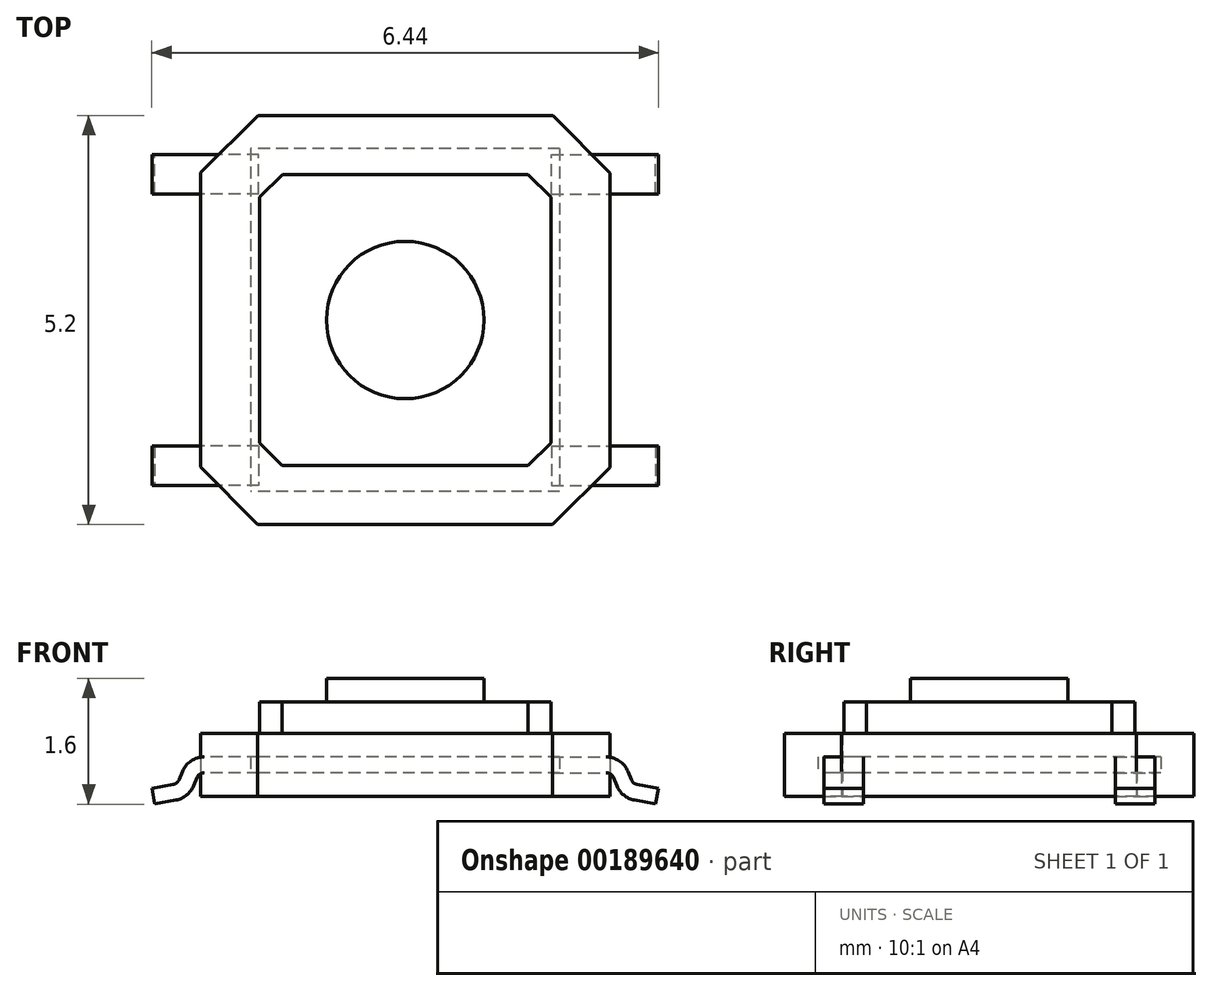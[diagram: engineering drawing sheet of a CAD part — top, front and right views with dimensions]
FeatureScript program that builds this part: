
annotation { "Feature Type Name" : "Feature", "Feature Type Description" : "" }
export const myFeature = defineFeature(function(context is Context, id is Id, definition is map)
    precondition{}
    {
        {
            var Q0;
            Q0=qCreatedBy(makeId("Top.planeOp"),FACE);
            var sketch = newSketch(context, id + "F0", { "sketchPlane" : qUnion([Q0])});
            skLineSegment(sketch, "E0", {"start": v(0, 2.6) * mm, "end": v(0, 0) * mm});
            skLineSegment(sketch, "E1", {"start": v(0, 2.6) * mm, "end": v(-1.87, 2.6) * mm});
            skLineSegment(sketch, "E2", {"start": v(-1.87, 2.6) * mm, "end": v(-2.6, 1.88) * mm});
            skLineSegment(sketch, "E3", {"start": v(-2.6, 1.88) * mm, "end": v(-2.6, 0) * mm});
            skLineSegment(sketch, "E4", {"start": v(-2.6, 0) * mm, "end": v(0, 0) * mm});
            skLineSegment(sketch, "E5.1.0", {"start": v(-1.88, -2.6) * mm, "end": v(0, -2.6) * mm});
            skLineSegment(sketch, "E5.1.1", {"start": v(-2.6, -1.87) * mm, "end": v(-1.88, -2.6) * mm});
            skLineSegment(sketch, "E5.1.3", {"start": v(0, -2.6) * mm, "end": v(0, 0) * mm});
            skLineSegment(sketch, "E5.1.4", {"start": v(-2.6, 0) * mm, "end": v(-2.6, -1.87) * mm});
            skLineSegment(sketch, "E5.2.0", {"start": v(2.6, -1.88) * mm, "end": v(2.6, 0) * mm});
            skLineSegment(sketch, "E5.2.1", {"start": v(1.87, -2.6) * mm, "end": v(2.6, -1.88) * mm});
            skLineSegment(sketch, "E5.2.2", {"start": v(0, -2.6) * mm, "end": v(0, 0) * mm});
            skLineSegment(sketch, "E5.2.3", {"start": v(2.6, 0) * mm, "end": v(0, 0) * mm});
            skLineSegment(sketch, "E5.2.4", {"start": v(0, -2.6) * mm, "end": v(1.87, -2.6) * mm});
            skLineSegment(sketch, "E5.3.0", {"start": v(1.88, 2.6) * mm, "end": v(0, 2.6) * mm});
            skLineSegment(sketch, "E5.3.1", {"start": v(2.6, 1.87) * mm, "end": v(1.88, 2.6) * mm});
            skLineSegment(sketch, "E5.3.2", {"start": v(2.6, 0) * mm, "end": v(0, 0) * mm});
            skLineSegment(sketch, "E5.3.4", {"start": v(2.6, 0) * mm, "end": v(2.6, 1.87) * mm});
            skPoint(sketch, "E5.center", {"position": v(0, 0) * mm});
            skSolve(sketch);
        }
        {
            var Q0;
            Q0=qSketchRegion(id+"F0",true);
            extrude(context, id + "F1", {"entities" : qUnion([Q0]), "depth" : 0.8 * mm});
        }
        {
            var Q0;
            Q0=makeQuery(id+"F1.opExtrude","CAP_FACE",FACE,{"disambiguationData":[OSD([sQuery(id+"F0.wireOp",EDGE,"E1"),sQuery(id+"F0.wireOp",EDGE,"E2"),sQuery(id+"F0.wireOp",EDGE,"E3"),sQuery(id+"F0.wireOp",EDGE,"E5.1.0"),sQuery(id+"F0.wireOp",EDGE,"E5.1.1"),sQuery(id+"F0.wireOp",EDGE,"E5.1.4"),sQuery(id+"F0.wireOp",EDGE,"E5.2.0"),sQuery(id+"F0.wireOp",EDGE,"E5.2.1"),sQuery(id+"F0.wireOp",EDGE,"E5.2.4"),sQuery(id+"F0.wireOp",EDGE,"E5.3.0"),sQuery(id+"F0.wireOp",EDGE,"E5.3.1"),sQuery(id+"F0.wireOp",EDGE,"E5.3.4")])],"isStart":false});
            var sketch = newSketch(context, id + "F2", { "sketchPlane" : qUnion([Q0])});
            skLineSegment(sketch, "E6.0", {"start": v(1.85, -1.56) * mm, "end": v(1.85, 1.56) * mm});
            skLineSegment(sketch, "E6.1", {"start": v(1.56, -1.85) * mm, "end": v(1.85, -1.56) * mm});
            skLineSegment(sketch, "E6.2", {"start": v(-1.56, -1.85) * mm, "end": v(1.56, -1.85) * mm});
            skLineSegment(sketch, "E6.3", {"start": v(-1.85, -1.56) * mm, "end": v(-1.56, -1.85) * mm});
            skLineSegment(sketch, "E6.4", {"start": v(-1.85, 1.56) * mm, "end": v(-1.85, -1.56) * mm});
            skLineSegment(sketch, "E6.5", {"start": v(1.85, 1.56) * mm, "end": v(1.56, 1.85) * mm});
            skLineSegment(sketch, "E6.6", {"start": v(-1.56, 1.85) * mm, "end": v(-1.85, 1.56) * mm});
            skLineSegment(sketch, "E6.7", {"start": v(1.56, 1.85) * mm, "end": v(-1.56, 1.85) * mm});
            skSolve(sketch);
        }
        {
            var Q0;
            Q0=qSketchRegion(id+"F2",true);
            extrude(context, id + "F3", {"entities" : qUnion([Q0]), "operationType" : NewBodyOperationType.ADD, "depth" : 0.4 * mm});
        }
        {
            var Q0;
            Q0=makeQuery(id+"F3.opExtrude","CAP_FACE",FACE,{"disambiguationData":[OSD([sQuery(id+"F2.wireOp",EDGE,"E6.0"),sQuery(id+"F2.wireOp",EDGE,"E6.1"),sQuery(id+"F2.wireOp",EDGE,"E6.2"),sQuery(id+"F2.wireOp",EDGE,"E6.3"),sQuery(id+"F2.wireOp",EDGE,"E6.4"),sQuery(id+"F2.wireOp",EDGE,"E6.5"),sQuery(id+"F2.wireOp",EDGE,"E6.6"),sQuery(id+"F2.wireOp",EDGE,"E6.7")])],"isStart":false});
            var sketch = newSketch(context, id + "F4", { "sketchPlane" : qUnion([Q0])});
            skCircle(sketch, "E7", {"center": v(0, 0) * mm, "radius": 1 * mm});
            skSolve(sketch);
        }
        {
            var Q0;
            Q0=qSketchRegion(id+"F4",true);
            extrude(context, id + "F5", {"entities" : qUnion([Q0]), "operationType" : NewBodyOperationType.ADD, "depth" : 0.3 * mm});
        }
        {
            var Q0;
            Q0=qCreatedBy(makeId("Top.planeOp"),FACE);
            cPlane(context, id + "F6", {"entities" : qUnion([Q0]), "cplaneType" : CPlaneType.OFFSET, "offset" : 0.3 * mm, "width" : 150 * mm, "height" : 150 * mm});
        }
        {
            var Q0;
            Q0=qCreatedBy(id+"F6.planeOp",FACE);
            var sketch = newSketch(context, id + "F7", { "sketchPlane" : qUnion([Q0])});
            skLineSegment(sketch, "E8.rect.bottom", {"start": v(1.96, 2.18) * mm, "end": v(-1.96, 2.18) * mm});
            skLineSegment(sketch, "E8.rect.top", {"start": v(1.96, -2.18) * mm, "end": v(-1.96, -2.18) * mm});
            skLineSegment(sketch, "E8.rect.left", {"start": v(1.96, 2.18) * mm, "end": v(1.96, -2.18) * mm});
            skLineSegment(sketch, "E8.rect.right", {"start": v(-1.96, 2.18) * mm, "end": v(-1.96, -2.18) * mm});
            skPoint(sketch, "E8.rect.middle", {"position": v(0, 0) * mm});
            skSolve(sketch);
        }
        {
            var Q0;
            Q0=qCreatedBy(makeId("Front.planeOp"),FACE);
            var sketch = newSketch(context, id + "F8", { "sketchPlane" : qUnion([Q0])});
            skLineSegment(sketch, "E9", {"start": v(1.86, 0.4) * mm, "end": v(2.55, 0.4) * mm});
            skLineSegment(sketch, "E10", {"start": v(2.74, 0.28) * mm, "end": v(2.78, 0.17) * mm});
            skLineSegment(sketch, "E11", {"start": v(2.93, 0.05) * mm, "end": v(3.2, 0) * mm});
            skPoint(sketch, "E12.visualSharp", {"position": v(2.68, 0.4) * mm});
            skArc(sketch, "E12.filletArc", {"start": v(2.74, 0.28) * mm, "mid": v(2.66, 0.37) * mm, "end": v(2.55, 0.4) * mm});
            skPoint(sketch, "E13.visualSharp", {"position": v(2.82, 0.07) * mm});
            skArc(sketch, "E13.filletArc", {"start": v(2.78, 0.17) * mm, "mid": v(2.84, 0.1) * mm, "end": v(2.93, 0.05) * mm});
            skSolve(sketch);
        }
        {
            var Q0;
            Q0=qSketchRegion(id+"F7",true);
            extrude(context, id + "F9", {"entities" : qUnion([Q0]), "depth" : 0.2 * mm});
        }
        {
            var Q0;
            Q0=sQuery(id+"F8.wireOp",EDGE,"E9");
            var Q1;
            Q1=sQuery(id+"F8.wireOp",VERTEX,"E9.start");
            cPlane(context, id + "F10", {"entities" : qUnion([Q0, Q1]), "cplaneType" : CPlaneType.LINE_POINT, "offset" : 150 * mm, "width" : 150 * mm, "height" : 150 * mm});
        }
        {
            var Q0;
            Q0=qCreatedBy(id+"F10.planeOp",FACE);
            var sketch = newSketch(context, id + "F11", { "sketchPlane" : qUnion([Q0])});
            skLineSegment(sketch, "E14.rect.bottom", {"start": v(-0.25, 0.3) * mm, "end": v(0.25, 0.3) * mm});
            skLineSegment(sketch, "E14.rect.top", {"start": v(-0.25, 0.5) * mm, "end": v(0.25, 0.5) * mm});
            skLineSegment(sketch, "E14.rect.left", {"start": v(-0.25, 0.3) * mm, "end": v(-0.25, 0.5) * mm});
            skLineSegment(sketch, "E14.rect.right", {"start": v(0.25, 0.3) * mm, "end": v(0.25, 0.5) * mm});
            skPoint(sketch, "E14.rect.middle", {"position": v(0, 0.4) * mm});
            skSolve(sketch);
        }
        {
            var Q0;
            Q0=qSketchRegion(id+"F11",true);
            var Q1;
            Q1=qConstructionFilter(qBodyType(qCreatedBy(id+"F8",EDGE),BodyType.WIRE),ConstructionObject.NO);
            sweep(context, id + "F12", {"profiles" : qUnion([Q0]), "path" : qUnion([Q1])});
        }
        {
            var Q0;
            Q0=makeQuery(id+"F12.opSweep","SWEPT_BODY",BODY,{"disambiguationData":[OSD([sQuery(id+"F8.wireOp",EDGE,"E9"),sQuery(id+"F11.wireOp",EDGE,"E14.rect.bottom"),sQuery(id+"F11.wireOp",EDGE,"E14.rect.top"),sQuery(id+"F11.wireOp",EDGE,"E14.rect.left"),sQuery(id+"F11.wireOp",EDGE,"E14.rect.right")])]});
            transform(context, id + "F13", {"entities" : qUnion([Q0]), "transformType" : TransformType.TRANSLATION_3D, "dx" : 0 * mm, "dy" : 1.85 * mm, "dz" : 0 * mm, "makeCopy" : false});
        }
        {
            var Q0;
            Q0=makeQuery(id+"F12.opSweep","SWEPT_BODY",BODY,{"disambiguationData":[OSD([sQuery(id+"F8.wireOp",EDGE,"E9"),sQuery(id+"F11.wireOp",EDGE,"E14.rect.bottom"),sQuery(id+"F11.wireOp",EDGE,"E14.rect.top"),sQuery(id+"F11.wireOp",EDGE,"E14.rect.left"),sQuery(id+"F11.wireOp",EDGE,"E14.rect.right")])]});
            var Q1;
            Q1=qCreatedBy(makeId("Right.planeOp"),FACE);
            mirror(context, id + "F14", {"entities" : qUnion([Q0]), "mirrorPlane" : qUnion([Q1])});
        }
        {
            var Q0;
            Q0=makeQuery(id+"F14.opPattern","COPY",BODY,{"derivedFrom":makeQuery(id+"F12.opSweep","SWEPT_BODY",BODY,{"disambiguationData":[OSD([sQuery(id+"F8.wireOp",EDGE,"E9"),sQuery(id+"F11.wireOp",EDGE,"E14.rect.bottom"),sQuery(id+"F11.wireOp",EDGE,"E14.rect.top"),sQuery(id+"F11.wireOp",EDGE,"E14.rect.left"),sQuery(id+"F11.wireOp",EDGE,"E14.rect.right")])]}),"instanceName":"1"});
            var Q1;
            Q1=makeQuery(id+"F12.opSweep","SWEPT_BODY",BODY,{"disambiguationData":[OSD([sQuery(id+"F8.wireOp",EDGE,"E9"),sQuery(id+"F11.wireOp",EDGE,"E14.rect.bottom"),sQuery(id+"F11.wireOp",EDGE,"E14.rect.top"),sQuery(id+"F11.wireOp",EDGE,"E14.rect.left"),sQuery(id+"F11.wireOp",EDGE,"E14.rect.right")])]});
            var Q2;
            Q2=qCreatedBy(makeId("Front.planeOp"),FACE);
            mirror(context, id + "F15", {"entities" : qUnion([Q0, Q1]), "mirrorPlane" : qUnion([Q2])});
        }
    });
